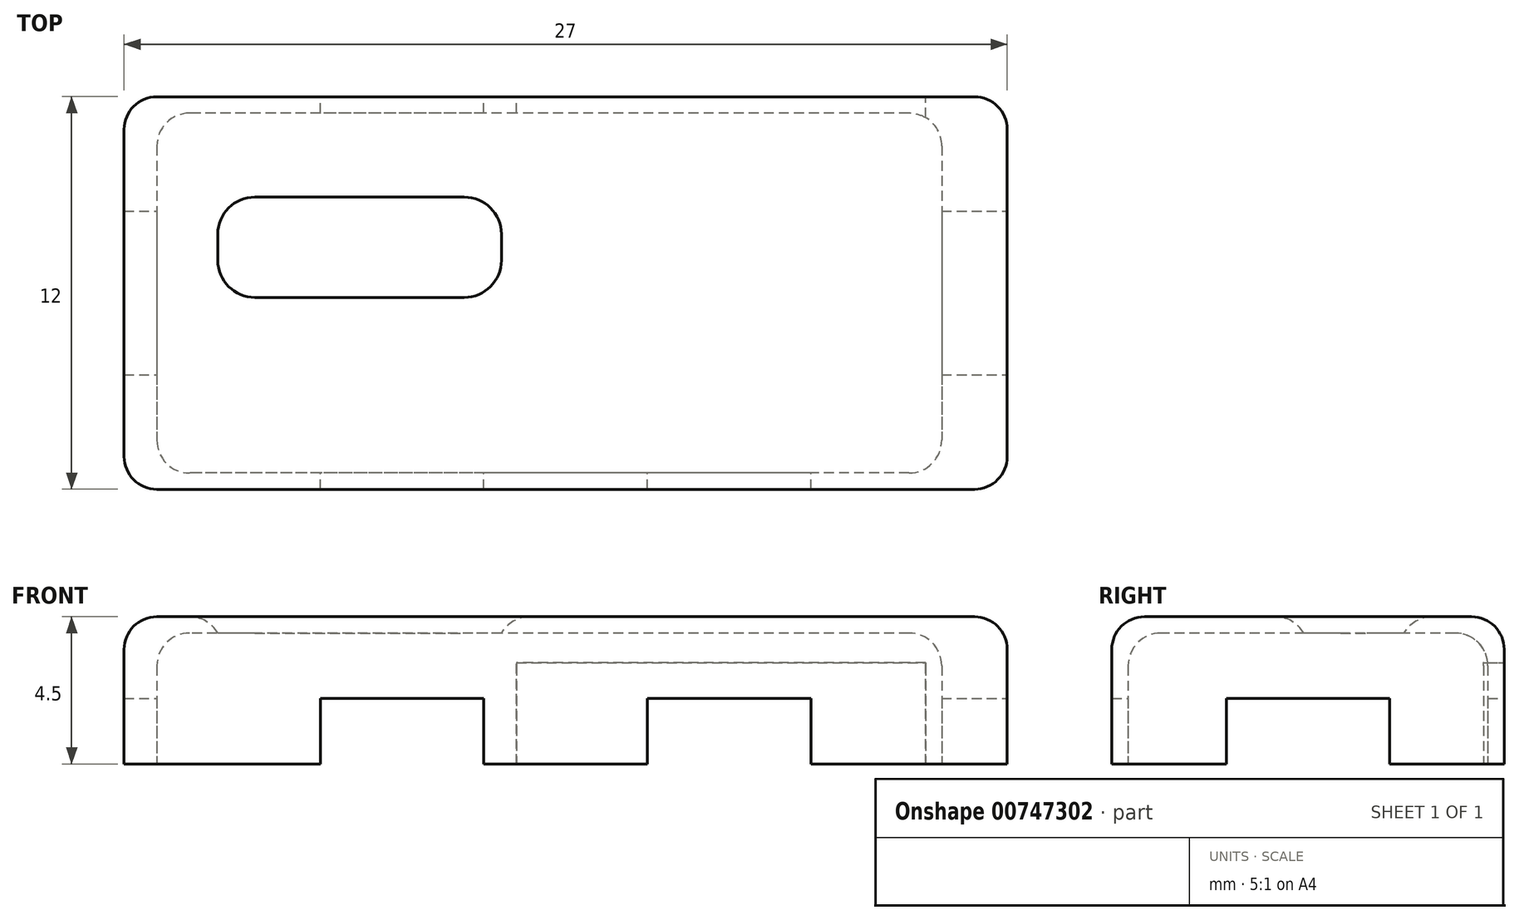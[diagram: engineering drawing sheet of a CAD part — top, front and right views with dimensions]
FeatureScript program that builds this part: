
annotation { "Feature Type Name" : "Feature", "Feature Type Description" : "" }
export const myFeature = defineFeature(function(context is Context, id is Id, definition is map)
    precondition{}
    {
        {
            var Q0;
            Q0=qCreatedBy(makeId("Top.planeOp"),FACE);
            var sketch = newSketch(context, id + "F0", { "sketchPlane" : qUnion([Q0])});
            skLineSegment(sketch, "E0.bottom", {"start": v(1, 2.88) * mm, "end": v(26, 2.88) * mm});
            skLineSegment(sketch, "E0.top", {"start": v(1, 14.88) * mm, "end": v(26, 14.88) * mm});
            skLineSegment(sketch, "E0.left", {"start": v(0, 3.88) * mm, "end": v(0, 13.88) * mm});
            skLineSegment(sketch, "E0.right", {"start": v(27, 3.88) * mm, "end": v(27, 13.88) * mm});
            skPoint(sketch, "E1.visualSharp", {"position": v(0, 14.88) * mm});
            skArc(sketch, "E1.filletArc", {"start": v(1, 14.88) * mm, "mid": v(0.3, 14.58) * mm, "end": v(0, 13.88) * mm});
            skPoint(sketch, "E2.visualSharp", {"position": v(27, 14.88) * mm});
            skArc(sketch, "E2.filletArc", {"start": v(27, 13.88) * mm, "mid": v(26.7, 14.58) * mm, "end": v(26, 14.88) * mm});
            skPoint(sketch, "E3.visualSharp", {"position": v(27, 2.88) * mm});
            skArc(sketch, "E3.filletArc", {"start": v(26, 2.88) * mm, "mid": v(26.7, 3.17) * mm, "end": v(27, 3.88) * mm});
            skPoint(sketch, "E4.visualSharp", {"position": v(0, 2.88) * mm});
            skArc(sketch, "E4.filletArc", {"start": v(0, 3.88) * mm, "mid": v(0.3, 3.17) * mm, "end": v(1, 2.88) * mm});
            skLineSegment(sketch, "E5.bottom", {"start": v(4, 11.68) * mm, "end": v(10.4, 11.68) * mm});
            skLineSegment(sketch, "E5.top", {"start": v(4, 8.88) * mm, "end": v(10.4, 8.88) * mm});
            skLineSegment(sketch, "E5.left", {"start": v(3, 10.68) * mm, "end": v(3, 9.88) * mm});
            skLineSegment(sketch, "E5.right", {"start": v(11.4, 10.68) * mm, "end": v(11.4, 9.88) * mm});
            skPoint(sketch, "E6.visualSharp", {"position": v(3, 11.68) * mm});
            skArc(sketch, "E6.filletArc", {"start": v(4, 11.68) * mm, "mid": v(3.3, 11.38) * mm, "end": v(3, 10.68) * mm});
            skPoint(sketch, "E7.visualSharp", {"position": v(3, 8.88) * mm});
            skArc(sketch, "E7.filletArc", {"start": v(3, 9.88) * mm, "mid": v(3.3, 9.17) * mm, "end": v(4, 8.88) * mm});
            skPoint(sketch, "E8.visualSharp", {"position": v(11.4, 11.68) * mm});
            skArc(sketch, "E8.filletArc", {"start": v(11.4, 10.68) * mm, "mid": v(11.1, 11.38) * mm, "end": v(10.4, 11.68) * mm});
            skPoint(sketch, "E9.visualSharp", {"position": v(11.4, 8.88) * mm});
            skArc(sketch, "E9.filletArc", {"start": v(10.4, 8.88) * mm, "mid": v(11.1, 9.17) * mm, "end": v(11.4, 9.88) * mm});
            skSolve(sketch);
        }
        {
            var Q0;
            Q0=qSketchRegion(id+"F0",true);
            extrude(context, id + "F1", {"entities" : qUnion([Q0]), "depth" : 4.5 * mm, "offsetDistance" : 25 * mm});
        }
        {
            var Q0;
            Q0=makeQuery(id+"F1.opExtrude","CAP_FACE",FACE,{"disambiguationData":[OSD([sQuery(id+"F0.wireOp",EDGE,"E0.bottom"),sQuery(id+"F0.wireOp",EDGE,"E0.top"),sQuery(id+"F0.wireOp",EDGE,"E0.left"),sQuery(id+"F0.wireOp",EDGE,"E0.right")])],"isStart":false});
            fillet(context, id + "F2", {"entities" : qUnion([Q0]), "radius" : 1 * mm, "tangentPropagation" : true, "allowEdgeOverflow" : false});
        }
        {
            var Q0;
            Q0=qCreatedBy(makeId("Top.planeOp"),FACE);
            var sketch = newSketch(context, id + "F3", { "sketchPlane" : qUnion([Q0])});
            skLineSegment(sketch, "E10.bottom", {"start": v(24, 14.38) * mm, "end": v(2, 14.38) * mm});
            skLineSegment(sketch, "E10.top", {"start": v(24, 3.38) * mm, "end": v(2, 3.38) * mm});
            skLineSegment(sketch, "E10.left", {"start": v(25, 13.38) * mm, "end": v(25, 4.38) * mm});
            skLineSegment(sketch, "E10.right", {"start": v(1, 13.38) * mm, "end": v(1, 4.38) * mm});
            skLineSegment(sketch, "E11.bottom", {"start": v(14.5, 3.38) * mm, "end": v(27, 3.38) * mm});
            skPoint(sketch, "E12.visualSharp", {"position": v(1, 3.38) * mm});
            skArc(sketch, "E12.filletArc", {"start": v(1, 4.38) * mm, "mid": v(1.3, 3.67) * mm, "end": v(2, 3.38) * mm});
            skPoint(sketch, "E13.visualSharp", {"position": v(1, 14.38) * mm});
            skArc(sketch, "E13.filletArc", {"start": v(2, 14.38) * mm, "mid": v(1.3, 14.08) * mm, "end": v(1, 13.38) * mm});
            skPoint(sketch, "E14.visualSharp", {"position": v(25, 14.38) * mm});
            skArc(sketch, "E14.filletArc", {"start": v(25, 13.38) * mm, "mid": v(24.7, 14.08) * mm, "end": v(24, 14.38) * mm});
            skPoint(sketch, "E15.visualSharp", {"position": v(25, 3.38) * mm});
            skArc(sketch, "E15.filletArc", {"start": v(24, 3.38) * mm, "mid": v(24.7, 3.67) * mm, "end": v(25, 4.38) * mm});
            skSolve(sketch);
        }
        {
            var Q0;
            Q0=makeQuery(id+"F3.imprint","IMPRINT",FACE,{"disambiguationData":[TD([[makeQuery(id+"F3.imprint","IMPRINT",EDGE,{"derivedFrom":sQuery(id+"F3.wireOp",EDGE,"E10.bottom")}),1.0]])]});
            extrude(context, id + "F4", {"entities" : qUnion([Q0]), "operationType" : NewBodyOperationType.REMOVE, "depth" : 4 * mm, "offsetDistance" : 25 * mm});
        }
        {
            var Q0;
            Q0=qCreatedBy(makeId("Top.planeOp"),FACE);
            var sketch = newSketch(context, id + "F5", { "sketchPlane" : qUnion([Q0])});
            skLineSegment(sketch, "E16.bottom", {"start": v(12, 13.29) * mm, "end": v(24.5, 13.29) * mm});
            skLineSegment(sketch, "E16.top", {"start": v(12, 16.27) * mm, "end": v(24.5, 16.27) * mm});
            skLineSegment(sketch, "E16.left", {"start": v(12, 13.29) * mm, "end": v(12, 16.27) * mm});
            skLineSegment(sketch, "E16.right", {"start": v(24.5, 13.29) * mm, "end": v(24.5, 16.27) * mm});
            skSolve(sketch);
        }
        {
            var Q0;
            Q0=qSketchRegion(id+"F5",true);
            extrude(context, id + "F6", {"entities" : qUnion([Q0]), "operationType" : NewBodyOperationType.REMOVE, "depth" : 3.1 * mm, "offsetDistance" : 25 * mm});
        }
        {
            var Q0;
            Q0=makeQuery(id+"F4.boolean.opBoolean","COPY",EDGE,{"derivedFrom":makeQuery(id+"F4.opExtrude","CAP_EDGE",EDGE,{"disambiguationData":[OSD([sQuery(id+"F3.wireOp",EDGE,"E10.top")])],"isStart":false})});
            var Q1;
            Q1=makeQuery(id+"F4.boolean.opBoolean","COPY",EDGE,{"derivedFrom":makeQuery(id+"F4.opExtrude","CAP_EDGE",EDGE,{"disambiguationData":[OSD([sQuery(id+"F3.wireOp",EDGE,"E10.left")])],"isStart":false})});
            var Q2;
            Q2=makeQuery(id+"F4.boolean.opBoolean","COPY",EDGE,{"derivedFrom":makeQuery(id+"F4.opExtrude","CAP_EDGE",EDGE,{"disambiguationData":[OSD([sQuery(id+"F3.wireOp",EDGE,"E12.filletArc")])],"isStart":false})});
            var Q3;
            Q3=makeQuery(id+"F4.boolean.opBoolean","COPY",EDGE,{"derivedFrom":makeQuery(id+"F4.opExtrude","CAP_EDGE",EDGE,{"disambiguationData":[OSD([sQuery(id+"F3.wireOp",EDGE,"E10.right")])],"isStart":false})});
            var Q4;
            Q4=makeQuery(id+"F4.boolean.opBoolean","COPY",EDGE,{"derivedFrom":makeQuery(id+"F4.opExtrude","CAP_EDGE",EDGE,{"disambiguationData":[OSD([sQuery(id+"F3.wireOp",EDGE,"E10.bottom")])],"isStart":false})});
            var Q5;
            Q5=makeQuery(id+"F4.boolean.opBoolean","COPY",EDGE,{"derivedFrom":makeQuery(id+"F4.opExtrude","CAP_EDGE",EDGE,{"disambiguationData":[OSD([sQuery(id+"F3.wireOp",EDGE,"E13.filletArc")])],"isStart":false})});
            var Q6;
            Q6=makeQuery(id+"F4.boolean.opBoolean","COPY",EDGE,{"derivedFrom":makeQuery(id+"F4.opExtrude","CAP_EDGE",EDGE,{"disambiguationData":[OSD([sQuery(id+"F3.wireOp",EDGE,"E14.filletArc")])],"isStart":false})});
            var Q7;
            Q7=makeQuery(id+"F4.boolean.opBoolean","COPY",EDGE,{"derivedFrom":makeQuery(id+"F4.opExtrude","CAP_EDGE",EDGE,{"disambiguationData":[OSD([sQuery(id+"F3.wireOp",EDGE,"E15.filletArc")])],"isStart":false})});
            fillet(context, id + "F7", {"entities" : qUnion([Q0, Q1, Q2, Q3, Q4, Q5, Q6, Q7]), "radius" : 1 * mm, "tangentPropagation" : true, "allowEdgeOverflow" : false});
        }
        {
            var Q0;
            Q0=makeQuery(id+"F1.opExtrude","CAP_FACE",FACE,{"disambiguationData":[OSD([sQuery(id+"F0.wireOp",EDGE,"E0.bottom"),sQuery(id+"F0.wireOp",EDGE,"E0.top"),sQuery(id+"F0.wireOp",EDGE,"E0.left"),sQuery(id+"F0.wireOp",EDGE,"E0.right"),sQuery(id+"F0.wireOp",EDGE,"E1.filletArc"),sQuery(id+"F0.wireOp",EDGE,"E2.filletArc"),sQuery(id+"F0.wireOp",EDGE,"E3.filletArc"),sQuery(id+"F0.wireOp",EDGE,"E4.filletArc"),sQuery(id+"F0.wireOp",EDGE,"E5.bottom"),sQuery(id+"F0.wireOp",EDGE,"E5.top"),sQuery(id+"F0.wireOp",EDGE,"E5.left"),sQuery(id+"F0.wireOp",EDGE,"E5.right"),sQuery(id+"F0.wireOp",EDGE,"E6.filletArc"),sQuery(id+"F0.wireOp",EDGE,"E7.filletArc"),sQuery(id+"F0.wireOp",EDGE,"E8.filletArc"),sQuery(id+"F0.wireOp",EDGE,"E9.filletArc")])],"isStart":true});
            var sketch = newSketch(context, id + "F8", { "sketchPlane" : qUnion([Q0])});
            skLineSegment(sketch, "E17.bottom", {"start": v(0, -6.38) * mm, "end": v(1, -6.38) * mm});
            skLineSegment(sketch, "E17.top", {"start": v(0, -11.38) * mm, "end": v(1, -11.38) * mm});
            skLineSegment(sketch, "E17.left", {"start": v(0, -6.38) * mm, "end": v(0, -11.38) * mm});
            skLineSegment(sketch, "E17.right", {"start": v(1, -6.38) * mm, "end": v(1, -11.38) * mm});
            skLineSegment(sketch, "E18.bottom", {"start": v(25, -6.38) * mm, "end": v(27, -6.38) * mm});
            skLineSegment(sketch, "E18.top", {"start": v(25, -11.38) * mm, "end": v(27, -11.38) * mm});
            skLineSegment(sketch, "E18.left", {"start": v(25, -6.38) * mm, "end": v(25, -11.38) * mm});
            skLineSegment(sketch, "E18.right", {"start": v(27, -6.38) * mm, "end": v(27, -11.38) * mm});
            skLineSegment(sketch, "E19.bottom", {"start": v(6, -2.88) * mm, "end": v(11, -2.88) * mm});
            skLineSegment(sketch, "E19.top", {"start": v(6, -3.38) * mm, "end": v(11, -3.38) * mm});
            skLineSegment(sketch, "E19.left", {"start": v(6, -2.88) * mm, "end": v(6, -3.38) * mm});
            skLineSegment(sketch, "E19.right", {"start": v(11, -2.88) * mm, "end": v(11, -3.38) * mm});
            skLineSegment(sketch, "E20.bottom", {"start": v(16, -2.88) * mm, "end": v(21, -2.88) * mm});
            skLineSegment(sketch, "E20.top", {"start": v(16, -3.38) * mm, "end": v(21, -3.38) * mm});
            skLineSegment(sketch, "E20.left", {"start": v(16, -2.88) * mm, "end": v(16, -3.38) * mm});
            skLineSegment(sketch, "E20.right", {"start": v(21, -2.88) * mm, "end": v(21, -3.38) * mm});
            skLineSegment(sketch, "E21.bottom", {"start": v(6, -14.38) * mm, "end": v(11, -14.38) * mm});
            skLineSegment(sketch, "E21.top", {"start": v(6, -14.88) * mm, "end": v(11, -14.88) * mm});
            skLineSegment(sketch, "E21.left", {"start": v(6, -14.38) * mm, "end": v(6, -14.88) * mm});
            skLineSegment(sketch, "E21.right", {"start": v(11, -14.38) * mm, "end": v(11, -14.88) * mm});
            skSolve(sketch);
        }
        {
            var Q0;
            Q0=qSketchRegion(id+"F8",true);
            extrude(context, id + "F9", {"entities" : qUnion([Q0]), "operationType" : NewBodyOperationType.REMOVE, "oppositeDirection" : true, "depth" : 2 * mm, "offsetDistance" : 25 * mm});
        }
    });
